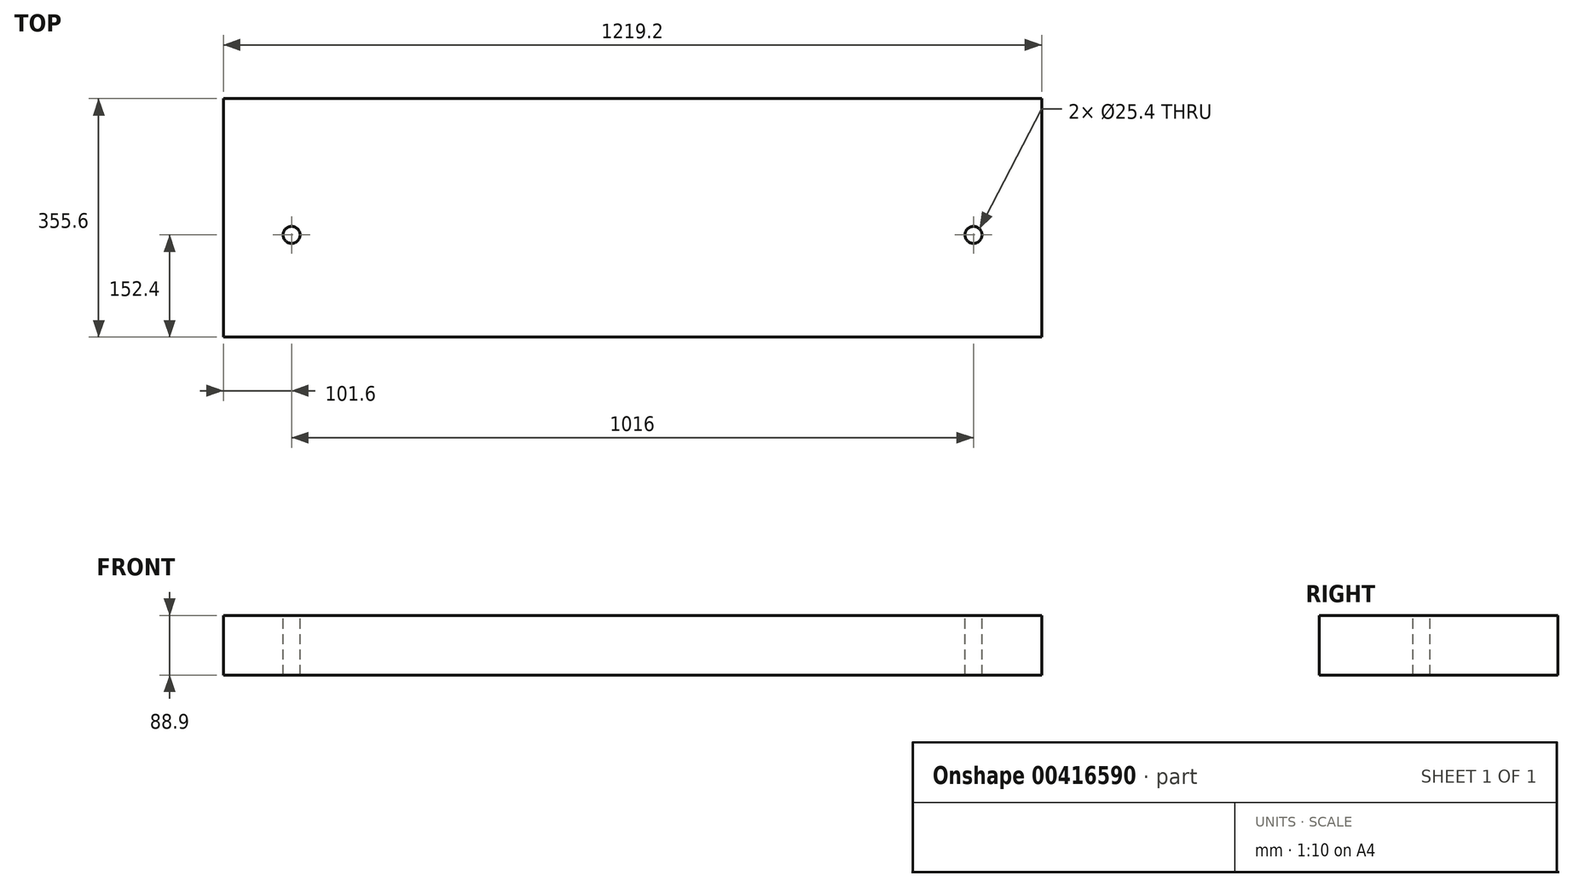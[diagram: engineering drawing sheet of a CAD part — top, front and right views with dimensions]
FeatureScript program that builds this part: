
annotation { "Feature Type Name" : "Feature", "Feature Type Description" : "" }
export const myFeature = defineFeature(function(context is Context, id is Id, definition is map)
    precondition{}
    {
        {
            var Q0;
            Q0=qCreatedBy(makeId("Top.planeOp"),FACE);
            var sketch = newSketch(context, id + "F0", { "sketchPlane" : qUnion([Q0])});
            skLineSegment(sketch, "E0.bottom", {"start": v(0, 0) * mm, "end": v(1219.2, 0) * mm});
            skLineSegment(sketch, "E0.top", {"start": v(0, 355.6) * mm, "end": v(1219.2, 355.6) * mm});
            skLineSegment(sketch, "E0.left", {"start": v(0, 0) * mm, "end": v(0, 355.6) * mm});
            skLineSegment(sketch, "E0.right", {"start": v(1219.2, 0) * mm, "end": v(1219.2, 355.6) * mm});
            skSolve(sketch);
        }
        {
            var Q0;
            Q0 = qSketchRegion(id + "F0", true);
            extrude(context, id + "F1", {"entities" : qUnion([Q0]), "depth" : 88.9 * mm, "offsetDistance" : 25.4 * mm});
        }
        {
            var Q0;
            Q0=makeQuery(id+"F1.opExtrude","CAP_FACE",FACE,{"disambiguationData":[OSD([sQuery(id+"F0.wireOp",EDGE,"E0.bottom"),sQuery(id+"F0.wireOp",EDGE,"E0.top"),sQuery(id+"F0.wireOp",EDGE,"E0.left"),sQuery(id+"F0.wireOp",EDGE,"E0.right")])],"isStart":false});
            var sketch = newSketch(context, id + "F2", { "sketchPlane" : qUnion([Q0])});
            skLineSegment(sketch, "E1", {"start": v(0, 152.4) * mm, "end": v(101.6, 152.4) * mm, "construction": true});
            skLineSegment(sketch, "E2", {"start": v(101.6, 152.4) * mm, "end": v(1117.6, 152.4) * mm, "construction": true});
            skLineSegment(sketch, "E3", {"start": v(1117.6, 152.4) * mm, "end": v(1219.2, 152.4) * mm, "construction": true});
            skCircle(sketch, "E4", {"center": v(101.6, 152.4) * mm, "radius": 12.7 * mm});
            skCircle(sketch, "E5", {"center": v(1117.6, 152.4) * mm, "radius": 12.7 * mm});
            skSolve(sketch);
        }
        {
            var Q0;
            Q0 = qSketchRegion(id + "F2", true);
            extrude(context, id + "F3", {"entities" : qUnion([Q0]), "operationType" : NewBodyOperationType.REMOVE, "endBound" : BoundingType.THROUGH_ALL, "oppositeDirection" : true, "depth" : 25.4 * mm, "offsetDistance" : 25.4 * mm});
        }
    });
